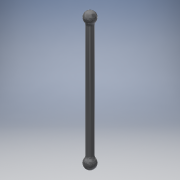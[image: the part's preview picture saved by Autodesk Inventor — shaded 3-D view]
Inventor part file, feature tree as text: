
AUTODESK INVENTOR PART (.ipt)
format: ipt  version: 2018 (Build 220112000, 112)  size: 119,808 bytes
history: native  units: mm
features: revolve x1, sketch x1
ambient origin geometry x8: Origin, YZ Plane, XZ Plane, XY Plane, X Axis, Y Axis, Z Axis, Center Point
bodies: Solid1 (feature_tree)
feature tree (2):
  revolve  "Revolution1"  [1 undecoded]
  sketch  "Sketch1"  dims[d0=5.0mm d1=1.5mm d2=25.75mm d3=2.0mm d4=90.0deg]
note: 1 required parameter value undecoded (feature->parameter linkage not recoverable at this tier; creation-order binding heuristic only, values carry confidence <= 0.55)
